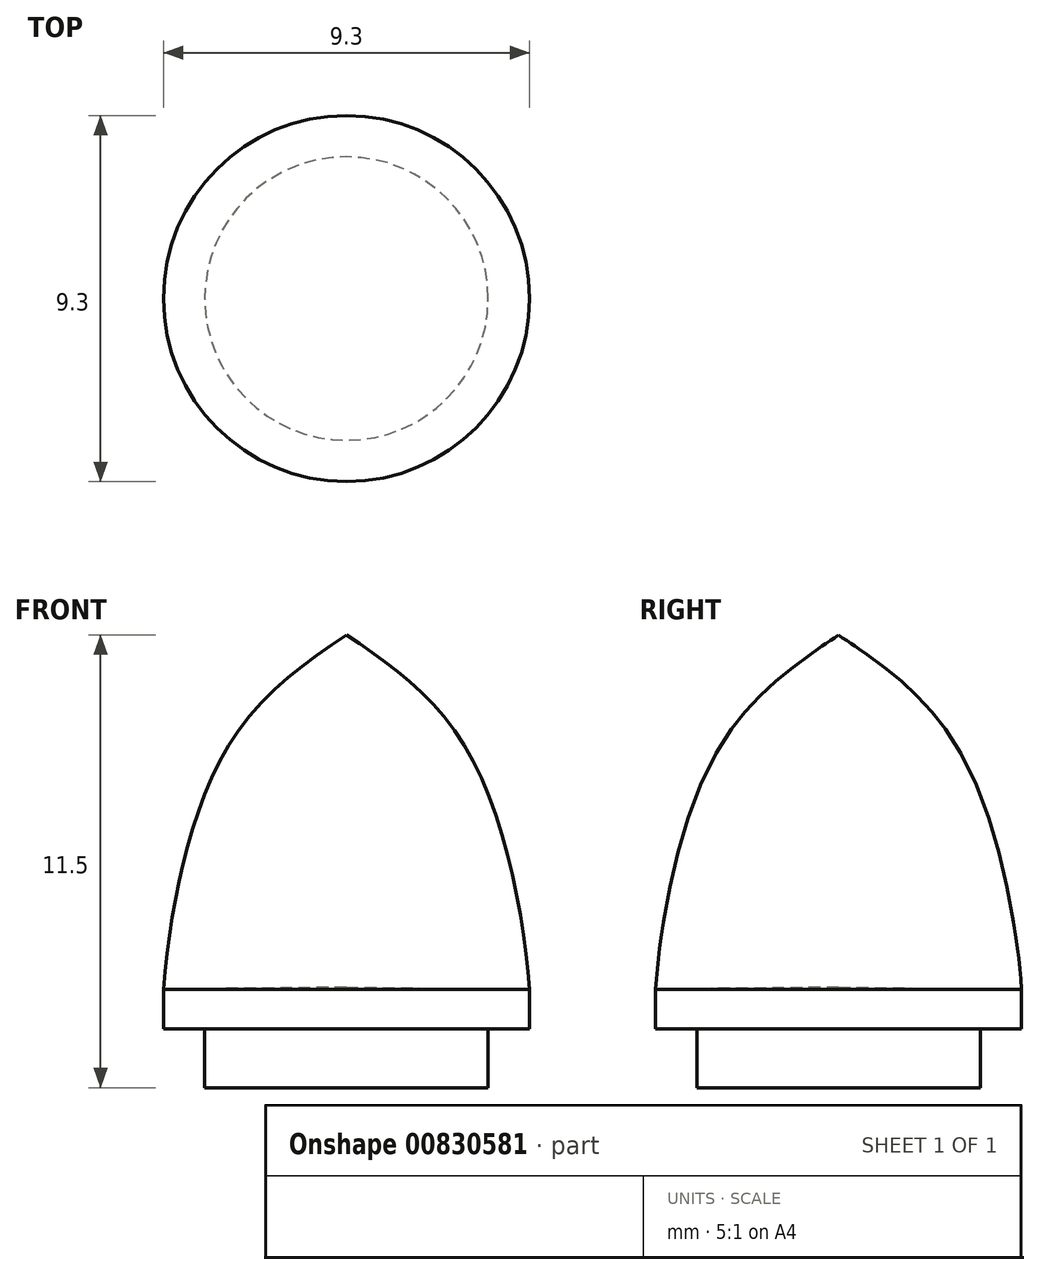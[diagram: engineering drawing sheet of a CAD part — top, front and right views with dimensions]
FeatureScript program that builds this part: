
annotation { "Feature Type Name" : "Feature", "Feature Type Description" : "" }
export const myFeature = defineFeature(function(context is Context, id is Id, definition is map)
    precondition{}
    {
        {
            var Q0;
            Q0=qCreatedBy(makeId("Top.planeOp"),FACE);
            var sketch = newSketch(context, id + "F0", { "sketchPlane" : qUnion([Q0])});
            skCircle(sketch, "E0", {"center": v(0, 0) * mm, "radius": 4.65 * mm});
            skCircle(sketch, "E1", {"center": v(0, 0) * mm, "radius": 3.6 * mm});
            skSolve(sketch);
        }
        {
            var Q0;
            Q0=makeQuery(id+"F0.imprint","IMPRINT",FACE,{"disambiguationData":[TD([[makeQuery(id+"F0.imprint","IMPRINT",EDGE,{"derivedFrom":sQuery(id+"F0.wireOp",EDGE,"E1")}),1.0]])]});
            extrude(context, id + "F1", {"entities" : qUnion([Q0]), "oppositeDirection" : true, "depth" : 1.5 * mm, "offsetDistance" : 25 * mm});
        }
        {
            var Q0;
            Q0=makeQuery(id+"F0.imprint","IMPRINT",FACE,{"disambiguationData":[TD([[makeQuery(id+"F0.imprint","IMPRINT",EDGE,{"derivedFrom":sQuery(id+"F0.wireOp",EDGE,"E0")}),1.0]])]});
            var Q1;
            Q1=makeQuery(id+"F0.imprint","IMPRINT",FACE,{"disambiguationData":[TD([[makeQuery(id+"F0.imprint","IMPRINT",EDGE,{"derivedFrom":sQuery(id+"F0.wireOp",EDGE,"E1")}),1.0]])]});
            extrude(context, id + "F2", {"entities" : qUnion([Q0, Q1]), "depth" : 1 * mm, "offsetDistance" : 25 * mm});
        }
        {
            var Q0;
            Q0=qCreatedBy(makeId("Front.planeOp"),FACE);
            var sketch = newSketch(context, id + "F3", { "sketchPlane" : qUnion([Q0])});
            skFitSpline(sketch, "E2", {"points": [v(0, 10) * mm, v(3.08, 7.04) * mm, v(4.65, 1) * mm], "startDerivative": vector(7.58, -5.04) * mm, "endDerivative": vector(0.7, -9.78) * mm});
            skLineSegment(sketch, "E3", {"start": v(0, 1.05) * mm, "end": v(0, 10) * mm});
            skLineSegment(sketch, "E4", {"start": v(0, 1.05) * mm, "end": v(4.65, 1) * mm});
            skSolve(sketch);
        }
        {
            var Q0;
            Q0 = qSketchRegion(id + "F3", true);
            var Q1;
            Q1=sQuery(id+"F3.wireOp",EDGE,"E3");
            revolve(context, id + "F4", {"surfaceOperationType" : NewSurfaceOperationType.NEW, "entities" : qUnion([Q0]), "axis" : qUnion([Q1]), "revolveType" : RevolveType.FULL});
        }
    });
